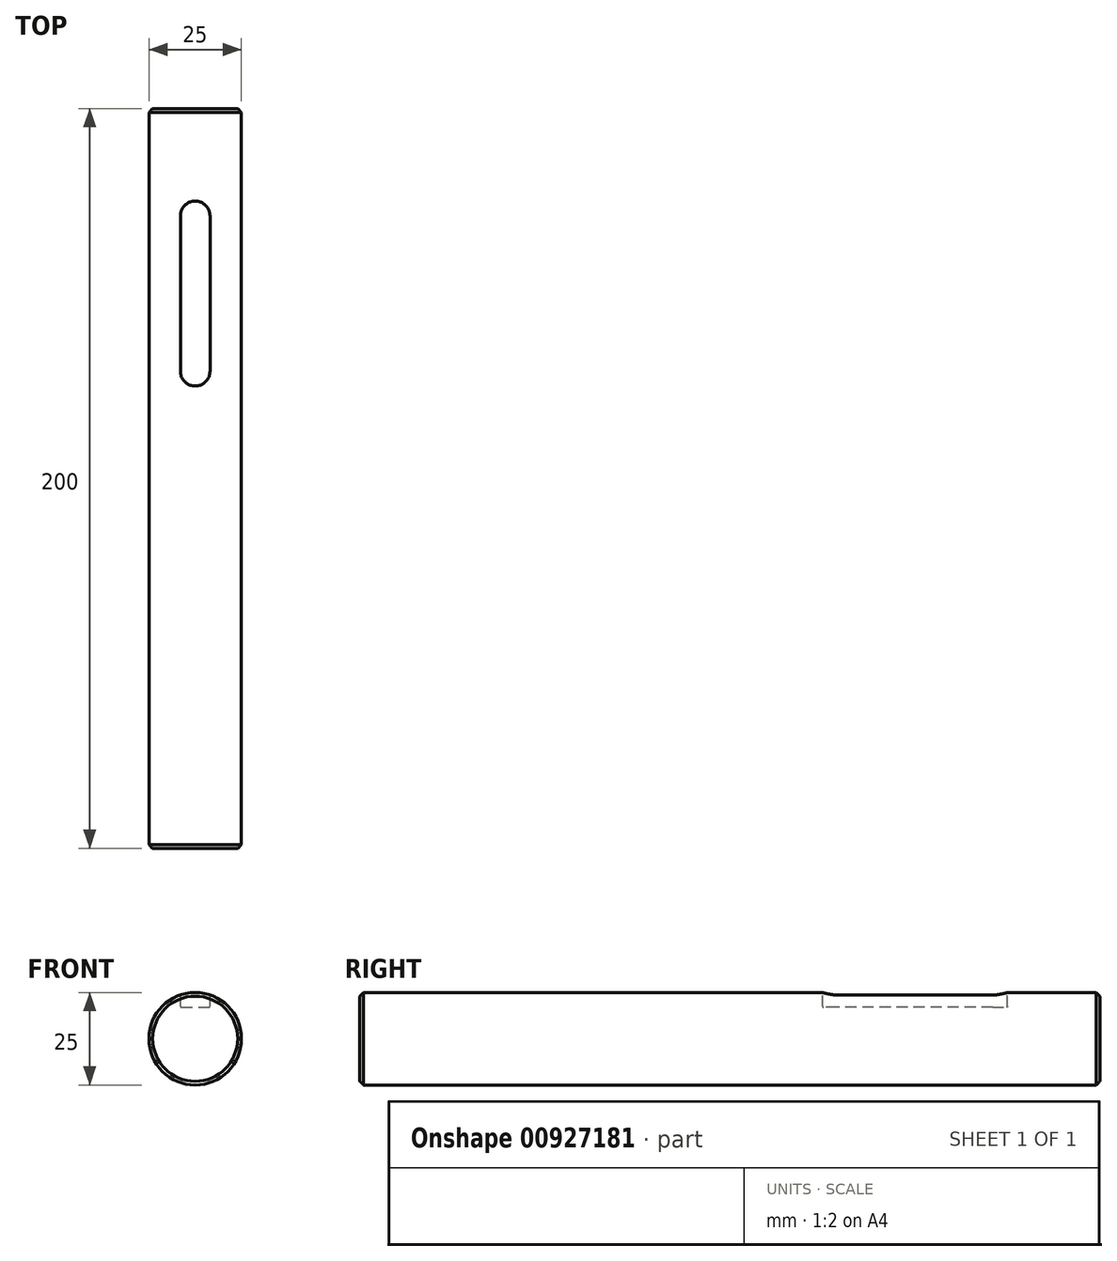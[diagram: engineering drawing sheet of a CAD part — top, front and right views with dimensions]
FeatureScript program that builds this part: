
annotation { "Feature Type Name" : "Feature", "Feature Type Description" : "" }
export const myFeature = defineFeature(function(context is Context, id is Id, definition is map)
    precondition{}
    {
        {
            var Q0;
            Q0=qCreatedBy(makeId("Front.planeOp"),FACE);
            var sketch = newSketch(context, id + "F0", { "sketchPlane" : qUnion([Q0])});
            skCircle(sketch, "E0", {"center": v(0, 0) * mm, "radius": 12.5 * mm});
            skSolve(sketch);
        }
        {
            var Q0;
            Q0 = qSketchRegion(id + "F0", true);
            extrude(context, id + "F1", {"entities" : qUnion([Q0]), "depth" : 200 * mm, "offsetDistance" : 25 * mm});
        }
        {
            var Q0;
            Q0=qCreatedBy(makeId("Top.planeOp"),FACE);
            cPlane(context, id + "F2", {"entities" : qUnion([Q0]), "cplaneType" : CPlaneType.OFFSET, "offset" : 12.5 * mm, "width" : 150 * mm, "height" : 150 * mm});
        }
        {
            var Q0;
            Q0=qCreatedBy(id+"F2.planeOp",FACE);
            var sketch = newSketch(context, id + "F3", { "sketchPlane" : qUnion([Q0])});
            skLineSegment(sketch, "E1.bottom", {"start": v(-4, -25) * mm, "end": v(4, -25) * mm});
            skLineSegment(sketch, "E1.top", {"start": v(-4, -75) * mm, "end": v(4, -75) * mm});
            skLineSegment(sketch, "E1.left", {"start": v(-4, -25) * mm, "end": v(-4, -75) * mm});
            skLineSegment(sketch, "E1.right", {"start": v(4, -25) * mm, "end": v(4, -75) * mm});
            skSolve(sketch);
        }
        {
            var Q0;
            Q0 = qSketchRegion(id + "F3", true);
            extrude(context, id + "F4", {"entities" : qUnion([Q0]), "operationType" : NewBodyOperationType.REMOVE, "oppositeDirection" : true, "depth" : 4 * mm, "offsetDistance" : 25 * mm});
        }
        {
            var Q0;
            Q0=makeQuery(id+"F4.boolean.opBoolean","COPY",EDGE,{"derivedFrom":makeQuery(id+"F4.opExtrude","SWEPT_EDGE",EDGE,{"disambiguationData":[OSD([sQuery(id+"F3.wireOp",EDGE,"E1.bottom"),sQuery(id+"F3.wireOp",EDGE,"E1.left")])]})});
            var Q1;
            Q1=makeQuery(id+"F4.boolean.opBoolean","COPY",EDGE,{"derivedFrom":makeQuery(id+"F4.opExtrude","SWEPT_EDGE",EDGE,{"disambiguationData":[OSD([sQuery(id+"F3.wireOp",EDGE,"E1.bottom"),sQuery(id+"F3.wireOp",EDGE,"E1.right")])]})});
            var Q2;
            Q2=makeQuery(id+"F4.boolean.opBoolean","COPY",EDGE,{"derivedFrom":makeQuery(id+"F4.opExtrude","SWEPT_EDGE",EDGE,{"disambiguationData":[OSD([sQuery(id+"F3.wireOp",EDGE,"E1.top"),sQuery(id+"F3.wireOp",EDGE,"E1.right")])]})});
            var Q3;
            Q3=makeQuery(id+"F4.boolean.opBoolean","COPY",EDGE,{"derivedFrom":makeQuery(id+"F4.opExtrude","SWEPT_EDGE",EDGE,{"disambiguationData":[OSD([sQuery(id+"F3.wireOp",EDGE,"E1.top"),sQuery(id+"F3.wireOp",EDGE,"E1.left")])]})});
            fillet(context, id + "F5", {"entities" : qUnion([Q0, Q1, Q2, Q3]), "radius" : 4 * mm, "tangentPropagation" : true, "allowEdgeOverflow" : false});
        }
        {
            var Q0;
            Q0=makeQuery(id+"F4.boolean.opBoolean","COPY",FACE,{"derivedFrom":makeQuery(id+"F4.opExtrude","CAP_FACE",FACE,{"disambiguationData":[OSD([sQuery(id+"F3.wireOp",EDGE,"E1.bottom"),sQuery(id+"F3.wireOp",EDGE,"E1.top"),sQuery(id+"F3.wireOp",EDGE,"E1.left"),sQuery(id+"F3.wireOp",EDGE,"E1.right")])],"isStart":false})});
            fillet(context, id + "F6", {"entities" : qUnion([Q0]), "radius" : .25 * mm, "tangentPropagation" : true, "allowEdgeOverflow" : false});
        }
        {
            var Q0;
            Q0=makeQuery(id+"F1.opExtrude","CAP_EDGE",EDGE,{"disambiguationData":[OSD([sQuery(id+"F0.wireOp",EDGE,"E0")])],"isStart":false});
            var Q1;
            Q1=makeQuery(id+"F1.opExtrude","CAP_EDGE",EDGE,{"disambiguationData":[OSD([sQuery(id+"F0.wireOp",EDGE,"E0")])],"isStart":true});
            chamfer(context, id + "F7", {"entities" : qUnion([Q0, Q1]), "width" : 1 * mm, "tangentPropagation" : true});
        }
    });
